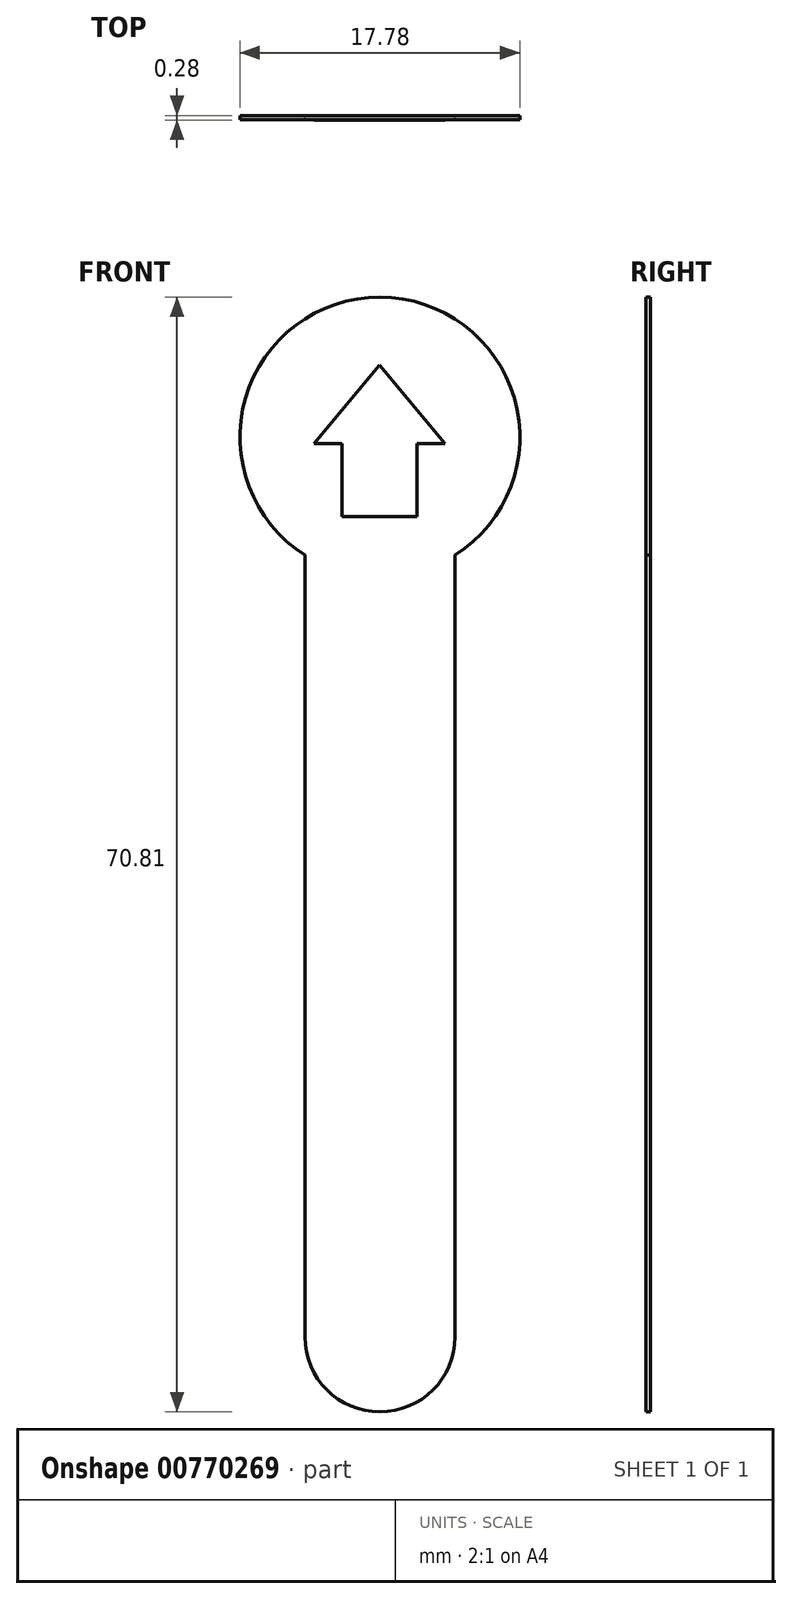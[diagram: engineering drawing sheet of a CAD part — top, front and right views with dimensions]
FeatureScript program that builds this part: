
annotation { "Feature Type Name" : "Feature", "Feature Type Description" : "" }
export const myFeature = defineFeature(function(context is Context, id is Id, definition is map)
    precondition{}
    {
        {
            var Q0;
            Q0=qCreatedBy(makeId("Front.planeOp"),FACE);
            var sketch = newSketch(context, id + "F0", { "sketchPlane" : qUnion([Q0])});
            skCircle(sketch, "E0", {"center": v(-0.05, 0) * mm, "radius": 8.89 * mm});
            skCircle(sketch, "E1", {"center": v(-0.05, -57.15) * mm, "radius": 4.76 * mm});
            skLineSegment(sketch, "E2", {"start": v(4.7, -57.15) * mm, "end": v(4.7, -7.5) * mm});
            skLineSegment(sketch, "E3", {"start": v(-4.81, -57.15) * mm, "end": v(-4.81, -7.5) * mm});
            skSolve(sketch);
        }
        {
            var Q0;
            Q0=qSketchRegion(id+"F0",true);
            extrude(context, id + "F1", {"entities" : qUnion([Q0]), "endBound" : BoundingType.SYMMETRIC, "depth" : 0.25 * mm});
        }
        {
            var Q0;
            Q0=makeQuery(id+"F1.opExtrude","CAP_FACE",FACE,{"disambiguationData":[OSD([sQuery(id+"F0.wireOp",EDGE,"E0"),sQuery(id+"F0.wireOp",EDGE,"E1"),sQuery(id+"F0.wireOp",EDGE,"E2"),sQuery(id+"F0.wireOp",EDGE,"E3")])],"isStart":false});
            var sketch = newSketch(context, id + "F2", { "sketchPlane" : qUnion([Q0])});
            skLineSegment(sketch, "E4", {"start": v(-2.46, -5.03) * mm, "end": v(2.29, -5.03) * mm});
            skLineSegment(sketch, "E5", {"start": v(2.29, -5.03) * mm, "end": v(2.29, -0.4) * mm});
            skLineSegment(sketch, "E6", {"start": v(2.29, -0.4) * mm, "end": v(4.07, -0.4) * mm});
            skLineSegment(sketch, "E7", {"start": v(4.07, -0.4) * mm, "end": v(-0.08, 4.57) * mm});
            skPoint(sketch, "E7.endSnap0", {"position": v(-0.08, -5.03) * mm});
            skLineSegment(sketch, "E8", {"start": v(-0.08, 4.57) * mm, "end": v(-4.23, -0.4) * mm});
            skPoint(sketch, "E8.endSnap0", {"position": v(3.18, -0.4) * mm});
            skLineSegment(sketch, "E9", {"start": v(-4.23, -0.4) * mm, "end": v(-2.46, -0.4) * mm});
            skLineSegment(sketch, "E10", {"start": v(-2.46, -0.4) * mm, "end": v(-2.46, -5.03) * mm});
            skSolve(sketch);
        }
        {
            var Q0;
            Q0=makeQuery(id+"F2.imprint","IMPRINT",FACE,{"disambiguationData":[TD([[makeQuery(id+"F2.imprint","IMPRINT",EDGE,{"derivedFrom":sQuery(id+"F2.wireOp",EDGE,"E4")}),1.0]])]});
            extrude(context, id + "F3", {"entities" : qUnion([Q0]), "depth" : 0.03 * mm});
        }
    });
